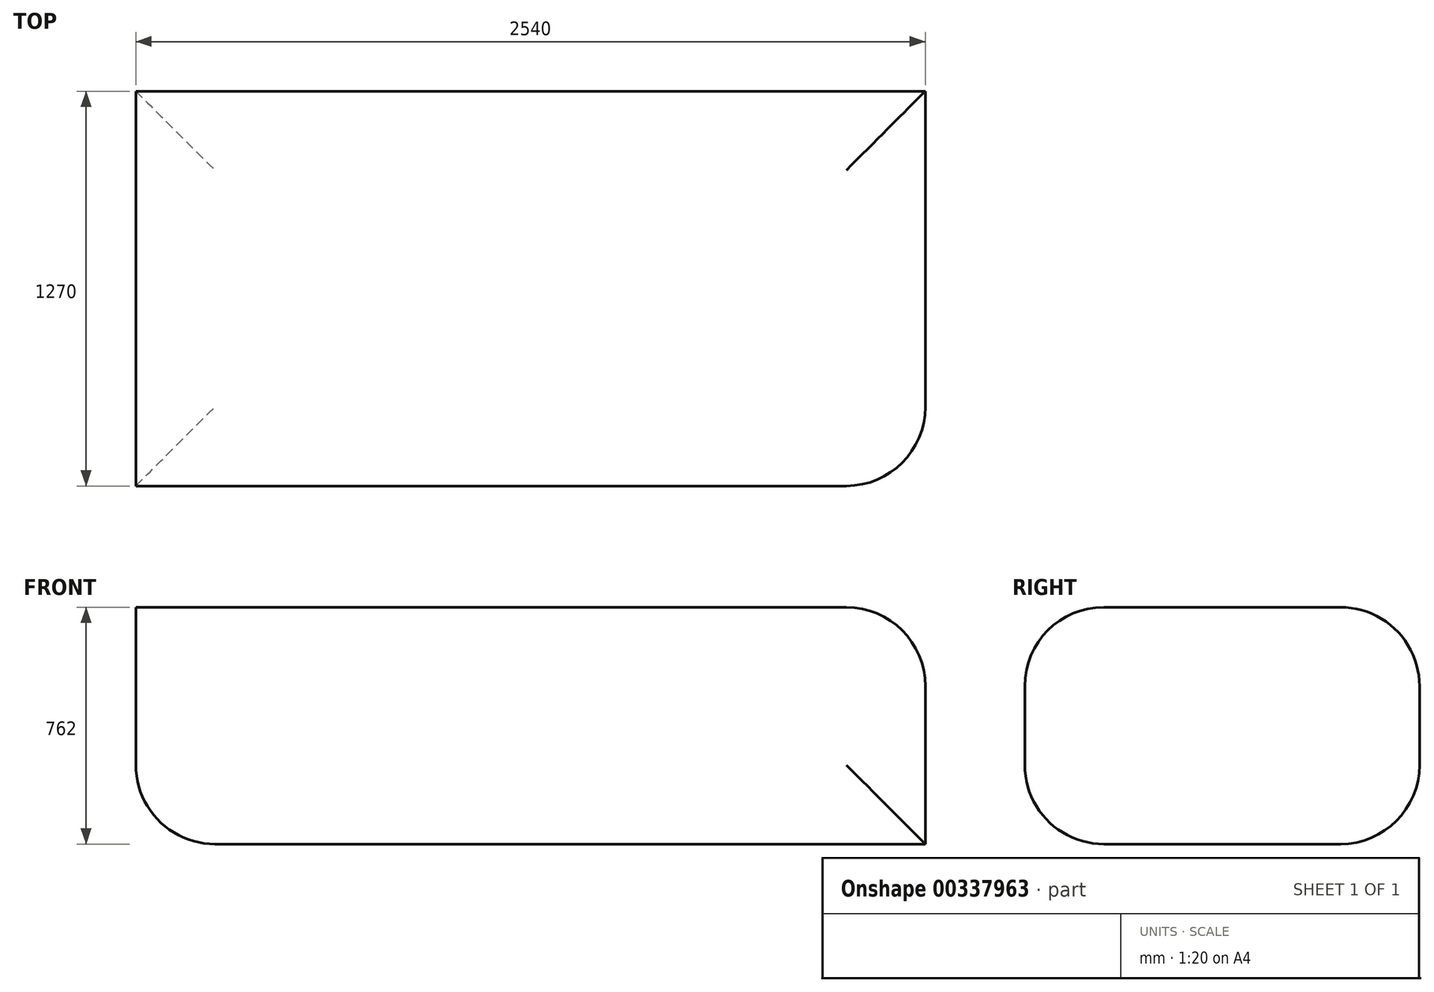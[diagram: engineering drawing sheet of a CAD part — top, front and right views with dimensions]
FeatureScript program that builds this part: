
annotation { "Feature Type Name" : "Feature", "Feature Type Description" : "" }
export const myFeature = defineFeature(function(context is Context, id is Id, definition is map)
    precondition{}
    {
        {
            var Q0;
            Q0=qCreatedBy(makeId("Top.planeOp"),FACE);
            var sketch = newSketch(context, id + "F0", { "sketchPlane" : qUnion([Q0])});
            skLineSegment(sketch, "E0.bottom", {"start": v(-2044.7, 1270) * mm, "end": v(495.3, 1270) * mm});
            skLineSegment(sketch, "E0.top", {"start": v(-2044.7, 0) * mm, "end": v(495.3, 0) * mm});
            skLineSegment(sketch, "E0.left", {"start": v(-2044.7, 1270) * mm, "end": v(-2044.7, 0) * mm});
            skLineSegment(sketch, "E0.right", {"start": v(495.3, 1270) * mm, "end": v(495.3, 0) * mm});
            skSolve(sketch);
        }
        {
            var Q0;
            Q0=makeQuery(id+"F0.imprint","IMPRINT",FACE,{"disambiguationData":[TD([[makeQuery(id+"F0.imprint","IMPRINT",EDGE,{"derivedFrom":sQuery(id+"F0.wireOp",EDGE,"E0.bottom")}),-1.0]])]});
            extrude(context, id + "F1", {"entities" : qUnion([Q0]), "depth" : 762 * mm});
        }
        {
            var Q0;
            Q0=makeQuery(id+"F1.opExtrude","CAP_EDGE",EDGE,{"disambiguationData":[OSD([sQuery(id+"F0.wireOp",EDGE,"E0.top")])],"isStart":false});
            var Q1;
            Q1=makeQuery(id+"F1.opExtrude","CAP_EDGE",EDGE,{"disambiguationData":[OSD([sQuery(id+"F0.wireOp",EDGE,"E0.right")])],"isStart":false});
            var Q2;
            Q2=makeQuery(id+"F1.opExtrude","CAP_EDGE",EDGE,{"disambiguationData":[OSD([sQuery(id+"F0.wireOp",EDGE,"E0.bottom")])],"isStart":false});
            var Q3;
            Q3=makeQuery(id+"F1.opExtrude","SWEPT_EDGE",EDGE,{"disambiguationData":[OSD([sQuery(id+"F0.wireOp",EDGE,"E0.top"),sQuery(id+"F0.wireOp",EDGE,"E0.right")])]});
            var Q4;
            Q4=makeQuery(id+"F1.opExtrude","CAP_EDGE",EDGE,{"disambiguationData":[OSD([sQuery(id+"F0.wireOp",EDGE,"E0.top")])],"isStart":true});
            var Q5;
            Q5=makeQuery(id+"F1.opExtrude","CAP_EDGE",EDGE,{"disambiguationData":[OSD([sQuery(id+"F0.wireOp",EDGE,"E0.bottom")])],"isStart":true});
            var Q6;
            Q6=makeQuery(id+"F1.opExtrude","CAP_EDGE",EDGE,{"disambiguationData":[OSD([sQuery(id+"F0.wireOp",EDGE,"E0.left")])],"isStart":true});
            fillet(context, id + "F2", {"entities" : qUnion([Q0, Q1, Q2, Q3, Q4, Q5, Q6]), "radius" : 254 * mm, "tangentPropagation" : true, "allowEdgeOverflow" : false});
        }
    });
